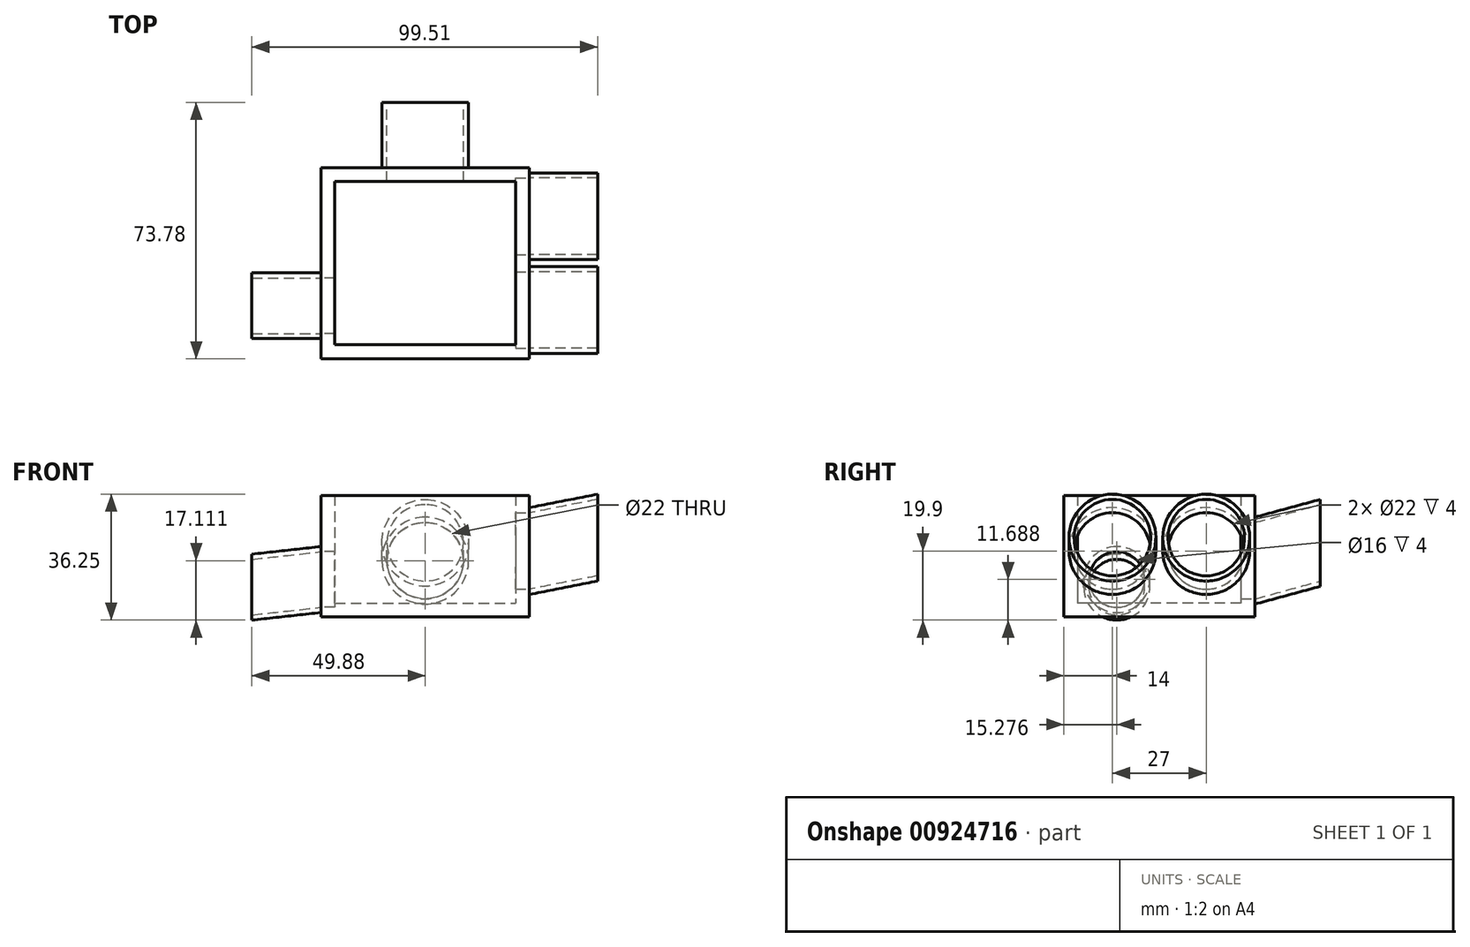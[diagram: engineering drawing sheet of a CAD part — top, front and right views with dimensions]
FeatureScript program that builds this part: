
annotation { "Feature Type Name" : "Feature", "Feature Type Description" : "" }
export const myFeature = defineFeature(function(context is Context, id is Id, definition is map)
    precondition{}
    {
        {
            var Q0;
            Q0=qCreatedBy(makeId("Top.planeOp"),FACE);
            var sketch = newSketch(context, id + "F0", { "sketchPlane" : qUnion([Q0])});
            skLineSegment(sketch, "E0.bottom", {"start": v(-30, 27.5) * mm, "end": v(30, 27.5) * mm});
            skLineSegment(sketch, "E0.top", {"start": v(-30, -27.5) * mm, "end": v(30, -27.5) * mm});
            skLineSegment(sketch, "E0.left", {"start": v(-30, 27.5) * mm, "end": v(-30, -27.5) * mm});
            skLineSegment(sketch, "E0.right", {"start": v(30, 27.5) * mm, "end": v(30, -27.5) * mm});
            skLineSegment(sketch, "E1", {"start": v(-30, 27.5) * mm, "end": v(30, -27.5) * mm, "construction": true});
            skLineSegment(sketch, "E2", {"start": v(-30, -27.5) * mm, "end": v(30, 27.5) * mm, "construction": true});
            skPoint(sketch, "E3", {"position": v(0, 0) * mm});
            skSolve(sketch);
        }
        {
            var Q0;
            Q0=makeQuery(id+"F0.imprint","IMPRINT",FACE,{"disambiguationData":[TD([[makeQuery(id+"F0.imprint","IMPRINT",EDGE,{"derivedFrom":sQuery(id+"F0.wireOp",EDGE,"E0.bottom")}),-1.0]])]});
            extrude(context, id + "F1", {"entities" : qUnion([Q0]), "depth" : 35 * mm, "offsetDistance" : 25 * mm});
        }
        {
            var Q0;
            Q0=makeQuery(id+"F1.opExtrude","CAP_FACE",FACE,{"disambiguationData":[OSD([sQuery(id+"F0.wireOp",EDGE,"E0.bottom"),sQuery(id+"F0.wireOp",EDGE,"E0.top"),sQuery(id+"F0.wireOp",EDGE,"E0.left"),sQuery(id+"F0.wireOp",EDGE,"E0.right")])],"isStart":false});
            shell(context, id + "F2", {"entities" : qUnion([Q0]), "thickness" : 4 * mm});
        }
        {
            var Q0;
            Q0=makeQuery(id+"F1.opExtrude","SWEPT_FACE",FACE,{"disambiguationData":[OSD([sQuery(id+"F0.wireOp",EDGE,"E0.left")])]});
            var sketch = newSketch(context, id + "F3", { "sketchPlane" : qUnion([Q0])});
            skCircle(sketch, "E4", {"center": v(12.22, 10.79) * mm, "radius": 8 * mm});
            skCircle(sketch, "E5", {"center": v(12.22, 10.79) * mm, "radius": 9.5 * mm});
            skSolve(sketch);
        }
        {
            var Q0;
            Q0=qCreatedBy(makeId("Front.planeOp"),FACE);
            var sketch = newSketch(context, id + "F4", { "sketchPlane" : qUnion([Q0])});
            skLineSegment(sketch, "E6", {"start": v(-30, 12.87) * mm, "end": v(-49.88, 10.69) * mm});
            skSolve(sketch);
        }
        {
            var Q0;
            Q0=qSketchRegion(id+"F3",true);
            var Q1;
            Q1=sQuery(id+"F3.wireOp",EDGE,"E5");
            var Q2;
            Q2=sQuery(id+"F3.wireOp",EDGE,"E4");
            var Q3;
            Q3=qConstructionFilter(qBodyType(qCreatedBy(id+"F4",EDGE),BodyType.WIRE),ConstructionObject.NO);
            sweep(context, id + "F5", {"profiles" : qUnion([Q0]), "surfaceProfiles" : qUnion([Q1, Q2]), "path" : qUnion([Q3])});
        }
        {
            var Q0;
            Q0=makeQuery(id+"F1.opExtrude","SWEPT_FACE",FACE,{"disambiguationData":[OSD([sQuery(id+"F0.wireOp",EDGE,"E0.left")])]});
            var sketch = newSketch(context, id + "F6", { "sketchPlane" : qUnion([Q0])});
            skCircle(sketch, "E7", {"center": v(12.22, 10.79) * mm, "radius": 8 * mm});
            skSolve(sketch);
        }
        {
            var Q0;
            Q0=qSketchRegion(id+"F6",true);
            var Q1;
            Q1=makeQuery(id+"F2.opShell","OFFSET_FACE",FACE,{"disambiguationData":[OSD([sQuery(id+"F0.wireOp",EDGE,"E0.left")])]});
            extrude(context, id + "F7", {"entities" : qUnion([Q0]), "operationType" : NewBodyOperationType.REMOVE, "endBound" : BoundingType.UP_TO_SURFACE, "oppositeDirection" : true, "depth" : 25 * mm, "endBoundEntityFace" : qUnion([Q1]), "offsetDistance" : 25 * mm});
        }
        {
            var Q0;
            Q0=makeQuery(id+"F1.opExtrude","SWEPT_FACE",FACE,{"disambiguationData":[OSD([sQuery(id+"F0.wireOp",EDGE,"E0.right")])]});
            var sketch = newSketch(context, id + "F8", { "sketchPlane" : qUnion([Q0])});
            skCircle(sketch, "E8", {"center": v(-13.5, 19) * mm, "radius": 11 * mm});
            skCircle(sketch, "E9", {"center": v(13.5, 19) * mm, "radius": 11 * mm});
            skCircle(sketch, "E10", {"center": v(-13.5, 19) * mm, "radius": 12.5 * mm});
            skCircle(sketch, "E11", {"center": v(13.5, 19) * mm, "radius": 12.5 * mm});
            skSolve(sketch);
        }
        {
            var Q0;
            Q0=qCreatedBy(makeId("Front.planeOp"),FACE);
            var sketch = newSketch(context, id + "F9", { "sketchPlane" : qUnion([Q0])});
            skLineSegment(sketch, "E12", {"start": v(34.94, 21.23) * mm, "end": v(54.57, 25.08) * mm});
            skSolve(sketch);
        }
        {
            var Q0;
            Q0=qSketchRegion(id+"F8",true);
            var Q1;
            Q1=qSketchRegion(id+"F9",true);
            var Q2;
            Q2=qConstructionFilter(qBodyType(qCreatedBy(id+"F9",EDGE),BodyType.WIRE),ConstructionObject.NO);
            sweep(context, id + "F10", {"operationType" : NewBodyOperationType.ADD, "profiles" : qUnion([Q0, Q1]), "path" : qUnion([Q2])});
        }
        {
            var Q0;
            {var subQ1=sQuery(id+"F0.wireOp",EDGE,"E0.right");var subQ3=sQuery(id+"F0.wireOp",EDGE,"E0.bottom");Q0=makeQuery(id+"F10.boolean.opBoolean","SPLIT",FACE,{"disambiguationData":[TD([makeQuery(id+"F1.opExtrude","SWEPT_FACE",FACE,{"disambiguationData":[OSD([subQ3])]})])],"derivedFrom":makeQuery(id+"F1.opExtrude","SWEPT_FACE",FACE,{"disambiguationData":[OSD([subQ1])]})});}
            var sketch = newSketch(context, id + "F11", { "sketchPlane" : qUnion([Q0])});
            skCircle(sketch, "E13", {"center": v(13.5, 19) * mm, "radius": 11 * mm});
            skCircle(sketch, "E14", {"center": v(-13.5, 19) * mm, "radius": 11 * mm});
            skSolve(sketch);
        }
        {
            var Q0;
            Q0=qSketchRegion(id+"F11",true);
            var Q1;
            Q1=makeQuery(id+"F2.opShell","OFFSET_FACE",FACE,{"disambiguationData":[OSD([sQuery(id+"F0.wireOp",EDGE,"E0.right")])]});
            extrude(context, id + "F12", {"entities" : qUnion([Q0]), "operationType" : NewBodyOperationType.REMOVE, "endBound" : BoundingType.UP_TO_SURFACE, "oppositeDirection" : true, "depth" : 25 * mm, "endBoundEntityFace" : qUnion([Q1]), "offsetDistance" : 25 * mm});
        }
        {
            var Q0;
            Q0=makeQuery(id+"F1.opExtrude","SWEPT_FACE",FACE,{"disambiguationData":[OSD([sQuery(id+"F0.wireOp",EDGE,"E0.bottom")])]});
            var sketch = newSketch(context, id + "F13", { "sketchPlane" : qUnion([Q0])});
            skCircle(sketch, "E15", {"center": v(0, 16.21) * mm, "radius": 12.5 * mm});
            skCircle(sketch, "E16", {"center": v(0, 16.21) * mm, "radius": 11 * mm});
            skSolve(sketch);
        }
        {
            var Q0;
            Q0=qCreatedBy(makeId("Right.planeOp"),FACE);
            var sketch = newSketch(context, id + "F14", { "sketchPlane" : qUnion([Q0])});
            skLineSegment(sketch, "E17", {"start": v(26.99, 16.32) * mm, "end": v(46.28, 21.59) * mm});
            skSolve(sketch);
        }
        {
            var Q0;
            Q0=qSketchRegion(id+"F13",true);
            var Q1;
            Q1=qConstructionFilter(qBodyType(qCreatedBy(id+"F14",EDGE),BodyType.WIRE),ConstructionObject.NO);
            sweep(context, id + "F15", {"operationType" : NewBodyOperationType.ADD, "profiles" : qUnion([Q0]), "path" : qUnion([Q1])});
        }
        {
            var Q0;
            Q0=makeQuery(id+"F15.boolean.opBoolean","SPLIT",FACE,{"disambiguationData":[TD([makeQuery(id+"F15.opSweep","SWEPT_FACE",FACE,{"disambiguationData":[OSD([sQuery(id+"F13.wireOp",EDGE,"E16"),sQuery(id+"F14.wireOp",EDGE,"E17")])]})])],"derivedFrom":makeQuery(id+"F1.opExtrude","SWEPT_FACE",FACE,{"disambiguationData":[OSD([sQuery(id+"F0.wireOp",EDGE,"E0.bottom")])]})});
            var Q1;
            Q1=makeQuery(id+"F2.opShell","OFFSET_FACE",FACE,{"disambiguationData":[OSD([sQuery(id+"F0.wireOp",EDGE,"E0.bottom")])]});
            extrude(context, id + "F16", {"entities" : qUnion([Q0]), "operationType" : NewBodyOperationType.REMOVE, "endBound" : BoundingType.UP_TO_SURFACE, "oppositeDirection" : true, "depth" : 25 * mm, "endBoundEntityFace" : qUnion([Q1]), "offsetDistance" : 25 * mm});
        }
    });
